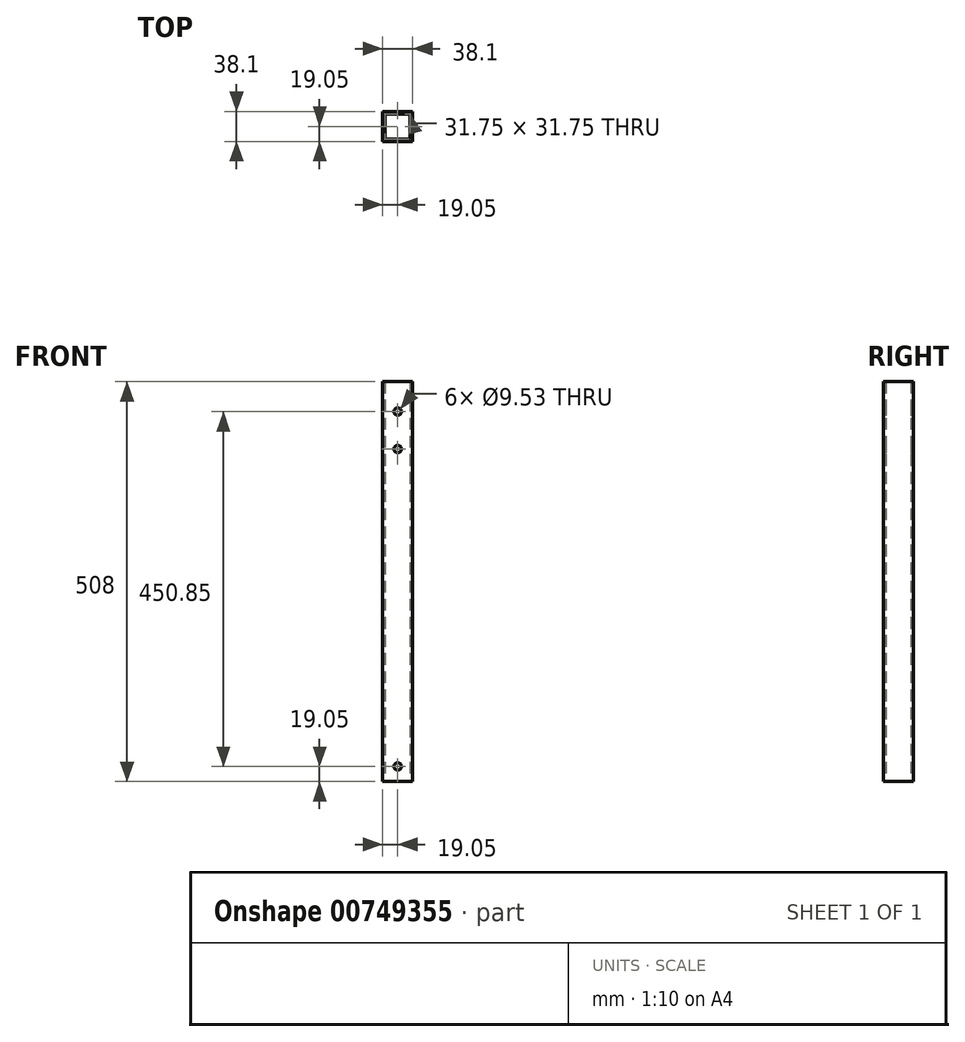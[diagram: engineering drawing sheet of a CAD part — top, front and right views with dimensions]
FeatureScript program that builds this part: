
annotation { "Feature Type Name" : "Feature", "Feature Type Description" : "" }
export const myFeature = defineFeature(function(context is Context, id is Id, definition is map)
    precondition{}
    {
        {
            var Q0;
            Q0=qCreatedBy(makeId("Top.planeOp"),FACE);
            var sketch = newSketch(context, id + "F0", { "sketchPlane" : qUnion([Q0])});
            skLineSegment(sketch, "E0.bottom", {"start": v(0, 0) * mm, "end": v(38.1, 0) * mm});
            skLineSegment(sketch, "E0.top", {"start": v(0, 38.1) * mm, "end": v(38.1, 38.1) * mm});
            skLineSegment(sketch, "E0.left", {"start": v(0, 0) * mm, "end": v(0, 38.1) * mm});
            skLineSegment(sketch, "E0.right", {"start": v(38.1, 0) * mm, "end": v(38.1, 38.1) * mm});
            skLineSegment(sketch, "E1.bottom", {"start": v(3.18, 3.17) * mm, "end": v(34.92, 3.17) * mm});
            skLineSegment(sketch, "E1.top", {"start": v(3.17, 34.93) * mm, "end": v(34.93, 34.93) * mm});
            skLineSegment(sketch, "E1.left", {"start": v(3.17, 3.18) * mm, "end": v(3.17, 34.93) * mm});
            skLineSegment(sketch, "E1.right", {"start": v(34.93, 3.18) * mm, "end": v(34.93, 34.93) * mm});
            skSolve(sketch);
        }
        {
            var Q0;
            Q0=makeQuery(id+"F0.imprint","IMPRINT",FACE,{"disambiguationData":[TD([[makeQuery(id+"F0.imprint","IMPRINT",EDGE,{"derivedFrom":sQuery(id+"F0.wireOp",EDGE,"E0.bottom")}),1.0]])]});
            extrude(context, id + "F1", {"entities" : qUnion([Q0]), "depth" : 508 * mm, "offsetDistance" : 25.4 * mm});
        }
        {
            var Q0;
            Q0=makeQuery(id+"F1.opExtrude","SWEPT_FACE",FACE,{"disambiguationData":[OSD([sQuery(id+"F0.wireOp",EDGE,"E0.bottom")])]});
            var sketch = newSketch(context, id + "F2", { "sketchPlane" : qUnion([Q0])});
            skCircle(sketch, "E2", {"center": v(19.05, 19.05) * mm, "radius": 4.76 * mm});
            skSolve(sketch);
        }
        {
            var Q0;
            Q0=makeQuery(id+"F2.imprint","IMPRINT",FACE,{"disambiguationData":[TD([[makeQuery(id+"F2.imprint","IMPRINT",EDGE,{"derivedFrom":sQuery(id+"F2.wireOp",EDGE,"E2")}),1.0]])]});
            extrude(context, id + "F3", {"entities" : qUnion([Q0]), "operationType" : NewBodyOperationType.REMOVE, "endBound" : BoundingType.THROUGH_ALL, "oppositeDirection" : true, "depth" : 25.4 * mm, "offsetDistance" : 25.4 * mm});
        }
        {
            var Q0;
            Q0=makeQuery(id+"F1.opExtrude","SWEPT_FACE",FACE,{"disambiguationData":[OSD([sQuery(id+"F0.wireOp",EDGE,"E0.bottom")])]});
            var sketch = newSketch(context, id + "F4", { "sketchPlane" : qUnion([Q0])});
            skCircle(sketch, "E3.0", {"center": v(19.05, 19.05) * mm, "radius": 4.76 * mm});
            skCircle(sketch, "E4", {"center": v(19.05, 422.28) * mm, "radius": 4.76 * mm});
            skSolve(sketch);
        }
        {
            var Q0;
            Q0=makeQuery(id+"F4.imprint","IMPRINT",FACE,{"disambiguationData":[TD([[makeQuery(id+"F4.imprint","IMPRINT",EDGE,{"derivedFrom":sQuery(id+"F4.wireOp",EDGE,"E4")}),1.0]])]});
            extrude(context, id + "F5", {"entities" : qUnion([Q0]), "operationType" : NewBodyOperationType.REMOVE, "endBound" : BoundingType.THROUGH_ALL, "oppositeDirection" : true, "depth" : 25.4 * mm, "offsetDistance" : 25.4 * mm});
        }
        {
            var Q0;
            Q0=makeQuery(id+"F1.opExtrude","SWEPT_FACE",FACE,{"disambiguationData":[OSD([sQuery(id+"F0.wireOp",EDGE,"E0.bottom")])]});
            var sketch = newSketch(context, id + "F6", { "sketchPlane" : qUnion([Q0])});
            skCircle(sketch, "E5.0", {"center": v(19.05, 422.28) * mm, "radius": 4.76 * mm});
            skCircle(sketch, "E6", {"center": v(19.05, 469.9) * mm, "radius": 4.76 * mm});
            skSolve(sketch);
        }
        {
            var Q0;
            Q0=makeQuery(id+"F6.imprint","IMPRINT",FACE,{"disambiguationData":[TD([[makeQuery(id+"F6.imprint","IMPRINT",EDGE,{"derivedFrom":sQuery(id+"F6.wireOp",EDGE,"E6")}),1.0]])]});
            extrude(context, id + "F7", {"entities" : qUnion([Q0]), "operationType" : NewBodyOperationType.REMOVE, "endBound" : BoundingType.THROUGH_ALL, "oppositeDirection" : true, "depth" : 25.4 * mm, "offsetDistance" : 25.4 * mm});
        }
    });
